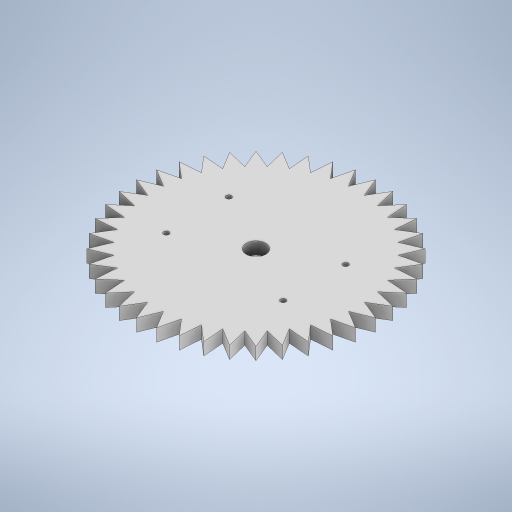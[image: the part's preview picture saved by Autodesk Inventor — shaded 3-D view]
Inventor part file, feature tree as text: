
AUTODESK INVENTOR PART (.ipt)
format: ipt  version: 2023 (Build 270158030, 158C)  size: 315,904 bytes
history: native  units: in
note: dims shown in document units (in); Inventor stores cm internally (conversion verified against a paired STEP export)
features: sketch x4, extrude x3, pattern_circular x1, hole x1
ambient origin geometry x8: Origin, YZ Plane, XZ Plane, XY Plane, X Axis, Y Axis, Z Axis, Center Point
bodies: Solid1 (feature_tree)
feature tree (9):
  extrude  "Extrusion1"  Depth=0.5in TaperAngle=0.0deg
  extrude  "Extrusion2"  Depth=0.7874in
  pattern_circular  "Circular Pattern1"  Count=40 Angle=360.0deg
  extrude  "Extrusion3"  Depth=0.3937in TaperAngle=0.0deg
  hole  "Hole1"  [1 undecoded]
  sketch  "Sketch1"  dims[d0=8.0in d1=0.5in d2=0.0in]
  sketch  "Sketch2"  dims[d3=45.0deg d4=0.7874in]
  sketch  "Sketch3"  dims[d5=0.0in d6=0.0in d7=15.748in d8=360.0deg]
  sketch  "Sketch5"  dims[d10=0.7874in d11=0.3937in d12=0.0in d15=0.2165in d16=0.2362in d17=0.1417in d18=0.0787in d19=90.0deg d20=0.315in d21=0.8108in d22=2.5in d23=4.68in]
note: 1 required parameter value undecoded (feature->parameter linkage not recoverable at this tier; creation-order binding heuristic only, values carry confidence <= 0.55)
